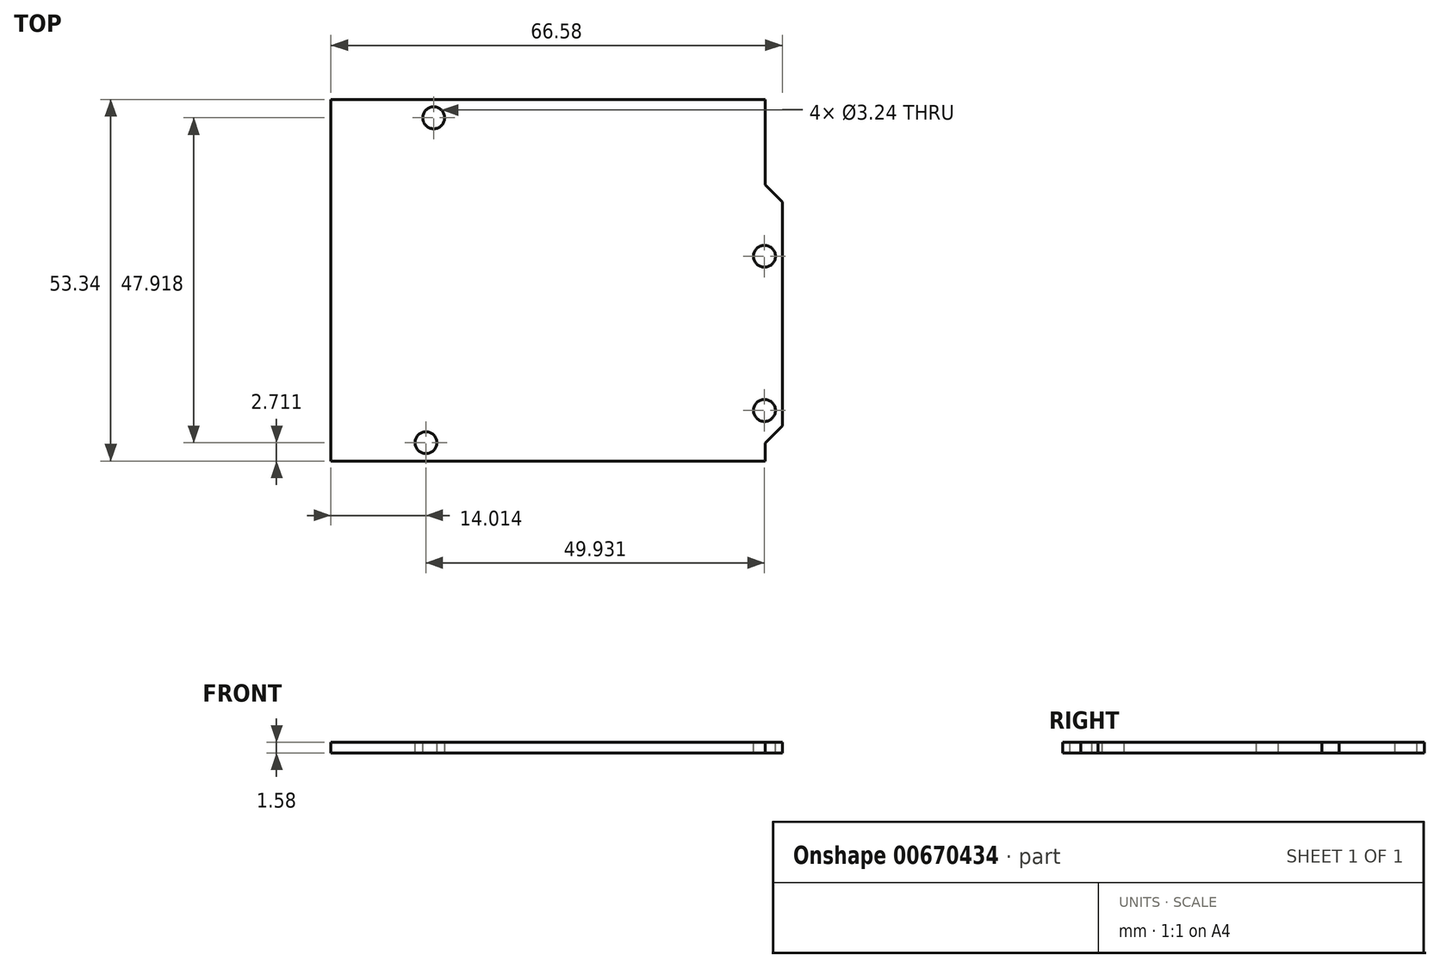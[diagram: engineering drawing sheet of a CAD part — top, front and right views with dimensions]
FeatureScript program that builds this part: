
annotation { "Feature Type Name" : "Feature", "Feature Type Description" : "" }
export const myFeature = defineFeature(function(context is Context, id is Id, definition is map)
    precondition{}
    {
        {
            var Q0;
            Q0=qCreatedBy(makeId("Top.planeOp"),FACE);
            var sketch = newSketch(context, id + "F0", { "sketchPlane" : qUnion([Q0])});
            skLineSegment(sketch, "E0", {"start": v(-32.02, 26.67) * mm, "end": v(32.02, 26.67) * mm});
            skLineSegment(sketch, "E1", {"start": v(32.02, 26.67) * mm, "end": v(32.02, 14.1) * mm});
            skLineSegment(sketch, "E2", {"start": v(32.02, -26.67) * mm, "end": v(-32.02, -26.67) * mm});
            skLineSegment(sketch, "E3", {"start": v(-32.02, -26.67) * mm, "end": v(-32.02, 26.67) * mm});
            skLineSegment(sketch, "E4", {"start": v(32.02, 14.1) * mm, "end": v(34.56, 11.56) * mm});
            skLineSegment(sketch, "E5", {"start": v(34.56, 11.56) * mm, "end": v(34.56, -21.46) * mm});
            skLineSegment(sketch, "E6", {"start": v(34.56, -21.46) * mm, "end": v(32.02, -24) * mm});
            skLineSegment(sketch, "E7", {"start": v(0, 0) * mm, "end": v(0, 26.67) * mm, "construction": true});
            skLineSegment(sketch, "E8", {"start": v(0, 0) * mm, "end": v(-32.02, 0) * mm});
            skLineSegment(sketch, "E9", {"start": v(0, 0) * mm, "end": v(-32.02, 0) * mm, "construction": true});
            skLineSegment(sketch, "E10.trimOffspring", {"start": v(32.02, -24) * mm, "end": v(32.02, -26.67) * mm});
            skSolve(sketch);
        }
        {
            var Q0;
            {var subQ3=sQuery(id+"F0.wireOp",EDGE,"E0");Q0=makeQuery(id+"F0.imprint","IMPRINT",FACE,{"disambiguationData":[TD([[makeQuery(id+"F0.imprint","IMPRINT",EDGE,{"derivedFrom":subQ3}),-1.0]])]});}
            extrude(context, id + "F1", {"entities" : qUnion([Q0]), "endBound" : BoundingType.SYMMETRIC, "depth" : 1.59 * mm, "offsetDistance" : 25 * mm});
        }
        {
            var Q0;
            Q0=makeQuery(id+"F1.opExtrude","CAP_FACE",FACE,{"disambiguationData":[OSD([sQuery(id+"F0.wireOp",EDGE,"E0"),sQuery(id+"F0.wireOp",EDGE,"E1"),sQuery(id+"F0.wireOp",EDGE,"E2"),sQuery(id+"F0.wireOp",EDGE,"E3"),sQuery(id+"F0.wireOp",EDGE,"E4"),sQuery(id+"F0.wireOp",EDGE,"E5"),sQuery(id+"F0.wireOp",EDGE,"E6"),sQuery(id+"F0.wireOp",EDGE,"E10.trimOffspring")])],"isStart":false});
            var sketch = newSketch(context, id + "F2", { "sketchPlane" : qUnion([Q0])});
            skCircle(sketch, "E11", {"center": v(-16.86, 23.96) * mm, "radius": 1.62 * mm});
            skCircle(sketch, "E12", {"center": v(31.93, 3.54) * mm, "radius": 1.62 * mm});
            skCircle(sketch, "E13", {"center": v(31.93, -19.2) * mm, "radius": 1.62 * mm});
            skCircle(sketch, "E14", {"center": v(-18, -23.96) * mm, "radius": 1.62 * mm});
            skSolve(sketch);
        }
        {
            var Q0;
            Q0=makeQuery(id+"F2.imprint","IMPRINT",FACE,{"disambiguationData":[TD([[makeQuery(id+"F2.imprint","IMPRINT",EDGE,{"derivedFrom":sQuery(id+"F2.wireOp",EDGE,"E11")}),1.0]])]});
            var Q1;
            Q1=makeQuery(id+"F2.imprint","IMPRINT",FACE,{"disambiguationData":[TD([[makeQuery(id+"F2.imprint","IMPRINT",EDGE,{"derivedFrom":sQuery(id+"F2.wireOp",EDGE,"E14")}),1.0]])]});
            var Q2;
            Q2=makeQuery(id+"F2.imprint","IMPRINT",FACE,{"disambiguationData":[TD([[makeQuery(id+"F2.imprint","IMPRINT",EDGE,{"derivedFrom":sQuery(id+"F2.wireOp",EDGE,"E12")}),1.0]])]});
            var Q3;
            Q3=makeQuery(id+"F2.imprint","IMPRINT",FACE,{"disambiguationData":[TD([[makeQuery(id+"F2.imprint","IMPRINT",EDGE,{"derivedFrom":sQuery(id+"F2.wireOp",EDGE,"E13")}),1.0]])]});
            extrude(context, id + "F3", {"entities" : qUnion([Q0, Q1, Q2, Q3]), "operationType" : NewBodyOperationType.REMOVE, "oppositeDirection" : true, "depth" : 25 * mm, "offsetDistance" : 25 * mm});
        }
    });
